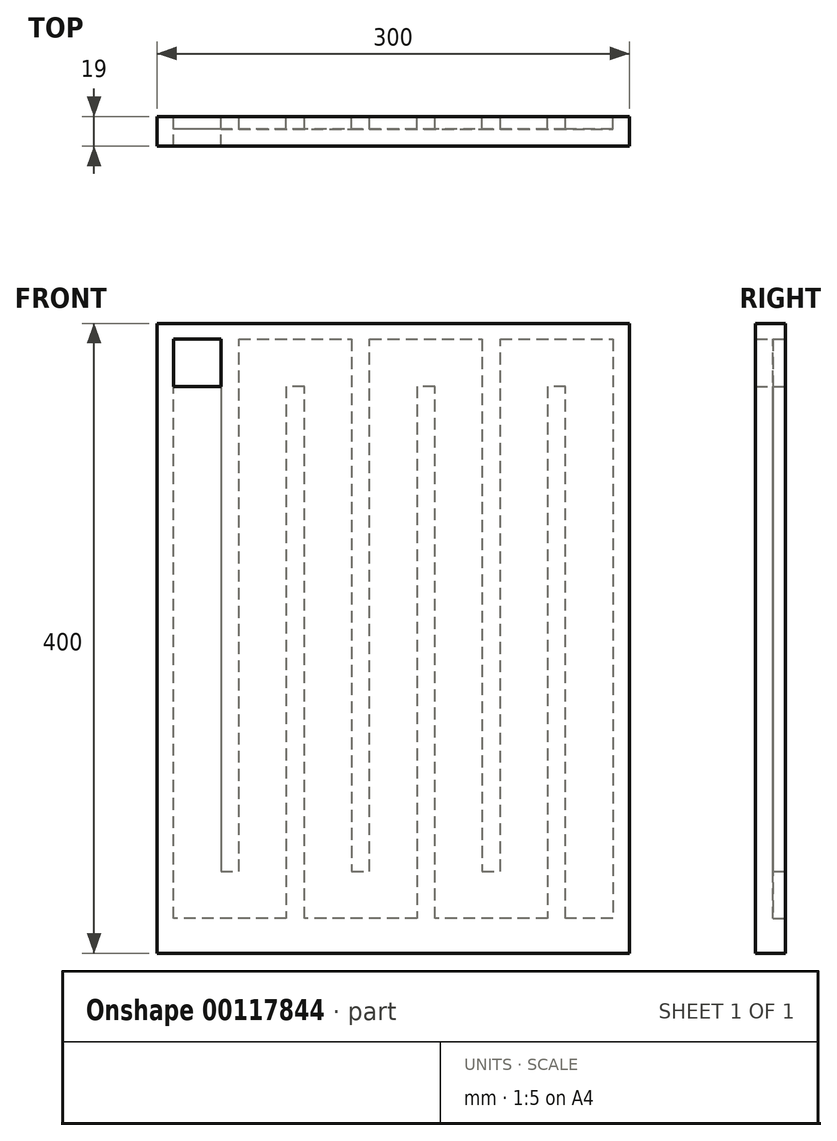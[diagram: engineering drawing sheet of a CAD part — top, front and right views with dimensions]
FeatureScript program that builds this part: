
annotation { "Feature Type Name" : "Feature", "Feature Type Description" : "" }
export const myFeature = defineFeature(function(context is Context, id is Id, definition is map)
    precondition{}
    {
        {
            var Q0;
            Q0=qCreatedBy(makeId("Front.planeOp"),FACE);
            var sketch = newSketch(context, id + "F0", { "sketchPlane" : qUnion([Q0])});
            skLineSegment(sketch, "E0.bottom", {"start": v(-164.03, 210.17) * mm, "end": v(135.97, 210.17) * mm});
            skLineSegment(sketch, "E0.top", {"start": v(-164.03, -189.83) * mm, "end": v(135.97, -189.83) * mm});
            skLineSegment(sketch, "E0.left", {"start": v(-164.03, 210.17) * mm, "end": v(-164.03, -189.83) * mm});
            skLineSegment(sketch, "E0.right", {"start": v(135.97, 210.17) * mm, "end": v(135.97, -189.83) * mm});
            skSolve(sketch);
        }
        {
            var Q0;
            Q0 = qSketchRegion(id + "F0", true);
            extrude(context, id + "F1", {"entities" : qUnion([Q0]), "depth" : 19 * mm});
        }
        {
            var Q0;
            Q0=makeQuery(id+"F1.opExtrude","CAP_FACE",FACE,{"disambiguationData":[OSD([sQuery(id+"F0.wireOp",EDGE,"E0.bottom"),sQuery(id+"F0.wireOp",EDGE,"E0.top"),sQuery(id+"F0.wireOp",EDGE,"E0.left"),sQuery(id+"F0.wireOp",EDGE,"E0.right")])],"isStart":true});
            var sketch = newSketch(context, id + "F2", { "sketchPlane" : qUnion([Q0])});
            skLineSegment(sketch, "E1", {"start": v(-125.47, -167.83) * mm, "end": v(-95.47, -167.83) * mm});
            skLineSegment(sketch, "E2", {"start": v(-95.47, -167.83) * mm, "end": v(-95.47, 170.17) * mm});
            skLineSegment(sketch, "E3", {"start": v(-95.47, 170.17) * mm, "end": v(-83.97, 170.17) * mm});
            skLineSegment(sketch, "E4", {"start": v(-83.97, 170.17) * mm, "end": v(-83.97, -167.83) * mm});
            skLineSegment(sketch, "E5", {"start": v(-83.97, -167.83) * mm, "end": v(-12.47, -167.83) * mm});
            skLineSegment(sketch, "E6", {"start": v(-12.47, -167.83) * mm, "end": v(-12.47, 170.17) * mm});
            skLineSegment(sketch, "E7", {"start": v(-12.47, 170.17) * mm, "end": v(-0.97, 170.17) * mm});
            skLineSegment(sketch, "E8", {"start": v(-0.97, 170.17) * mm, "end": v(-0.97, -167.83) * mm});
            skLineSegment(sketch, "E9", {"start": v(-0.97, -167.83) * mm, "end": v(70.53, -167.83) * mm});
            skLineSegment(sketch, "E10", {"start": v(70.53, -167.83) * mm, "end": v(70.53, 170.17) * mm});
            skLineSegment(sketch, "E11", {"start": v(70.53, 170.17) * mm, "end": v(82.03, 170.17) * mm});
            skLineSegment(sketch, "E12", {"start": v(82.03, 170.17) * mm, "end": v(82.03, -167.83) * mm});
            skLineSegment(sketch, "E13", {"start": v(82.03, -167.83) * mm, "end": v(153.53, -167.83) * mm});
            skLineSegment(sketch, "E14", {"start": v(153.53, -167.83) * mm, "end": v(153.53, 200.17) * mm});
            skLineSegment(sketch, "E15", {"start": v(153.53, 200.17) * mm, "end": v(123.53, 200.17) * mm});
            skLineSegment(sketch, "E16", {"start": v(123.53, 200.17) * mm, "end": v(123.53, -137.83) * mm});
            skLineSegment(sketch, "E17", {"start": v(123.53, -137.83) * mm, "end": v(112.03, -137.83) * mm});
            skLineSegment(sketch, "E18", {"start": v(112.03, -137.83) * mm, "end": v(112.03, 200.17) * mm});
            skLineSegment(sketch, "E19", {"start": v(112.03, 200.17) * mm, "end": v(40.53, 200.17) * mm});
            skLineSegment(sketch, "E20", {"start": v(40.53, 200.17) * mm, "end": v(40.53, -137.83) * mm});
            skLineSegment(sketch, "E21", {"start": v(40.53, -137.83) * mm, "end": v(29.03, -137.83) * mm});
            skLineSegment(sketch, "E22", {"start": v(29.03, -137.83) * mm, "end": v(29.03, 200.17) * mm});
            skLineSegment(sketch, "E23", {"start": v(29.03, 200.17) * mm, "end": v(-42.47, 200.17) * mm});
            skLineSegment(sketch, "E24", {"start": v(-42.47, 200.17) * mm, "end": v(-42.47, -137.83) * mm});
            skLineSegment(sketch, "E25", {"start": v(-42.47, -137.83) * mm, "end": v(-53.97, -137.83) * mm});
            skLineSegment(sketch, "E26", {"start": v(-53.97, -137.83) * mm, "end": v(-53.97, 200.17) * mm});
            skLineSegment(sketch, "E27", {"start": v(-53.97, 200.17) * mm, "end": v(-125.47, 200.17) * mm});
            skLineSegment(sketch, "E28", {"start": v(-125.47, 200.17) * mm, "end": v(-125.47, -167.83) * mm});
            skSolve(sketch);
        }
        {
            var Q0;
            Q0 = qSketchRegion(id + "F2", true);
            extrude(context, id + "F3", {"entities" : qUnion([Q0]), "operationType" : NewBodyOperationType.REMOVE, "oppositeDirection" : true, "depth" : 8 * mm});
        }
        {
            var Q0;
            Q0=makeQuery(id+"F3.boolean.opBoolean","COPY",FACE,{"derivedFrom":makeQuery(id+"F3.opExtrude","CAP_FACE",FACE,{"disambiguationData":[OSD([sQuery(id+"F2.wireOp",EDGE,"E1"),sQuery(id+"F2.wireOp",EDGE,"E2"),sQuery(id+"F2.wireOp",EDGE,"E3"),sQuery(id+"F2.wireOp",EDGE,"E4"),sQuery(id+"F2.wireOp",EDGE,"E5"),sQuery(id+"F2.wireOp",EDGE,"E6"),sQuery(id+"F2.wireOp",EDGE,"E7"),sQuery(id+"F2.wireOp",EDGE,"E8"),sQuery(id+"F2.wireOp",EDGE,"E9"),sQuery(id+"F2.wireOp",EDGE,"E10"),sQuery(id+"F2.wireOp",EDGE,"E11"),sQuery(id+"F2.wireOp",EDGE,"E12"),sQuery(id+"F2.wireOp",EDGE,"E13"),sQuery(id+"F2.wireOp",EDGE,"E14"),sQuery(id+"F2.wireOp",EDGE,"E15"),sQuery(id+"F2.wireOp",EDGE,"E16"),sQuery(id+"F2.wireOp",EDGE,"E17"),sQuery(id+"F2.wireOp",EDGE,"E18"),sQuery(id+"F2.wireOp",EDGE,"E19"),sQuery(id+"F2.wireOp",EDGE,"E20"),sQuery(id+"F2.wireOp",EDGE,"E21"),sQuery(id+"F2.wireOp",EDGE,"E22"),sQuery(id+"F2.wireOp",EDGE,"E23"),sQuery(id+"F2.wireOp",EDGE,"E24"),sQuery(id+"F2.wireOp",EDGE,"E25"),sQuery(id+"F2.wireOp",EDGE,"E26"),sQuery(id+"F2.wireOp",EDGE,"E27"),sQuery(id+"F2.wireOp",EDGE,"E28")])],"isStart":false})});
            var sketch = newSketch(context, id + "F4", { "sketchPlane" : qUnion([Q0])});
            skLineSegment(sketch, "E29.bottom", {"start": v(123.53, 200.17) * mm, "end": v(153.53, 200.17) * mm});
            skLineSegment(sketch, "E29.top", {"start": v(123.53, 170.17) * mm, "end": v(153.53, 170.17) * mm});
            skLineSegment(sketch, "E29.left", {"start": v(123.53, 200.17) * mm, "end": v(123.53, 170.17) * mm});
            skLineSegment(sketch, "E29.right", {"start": v(153.53, 200.17) * mm, "end": v(153.53, 170.17) * mm});
            skSolve(sketch);
        }
        {
            var Q0;
            Q0 = qSketchRegion(id + "F4", true);
            extrude(context, id + "F5", {"entities" : qUnion([Q0]), "operationType" : NewBodyOperationType.REMOVE, "oppositeDirection" : true, "depth" : 11 * mm});
        }
    });
